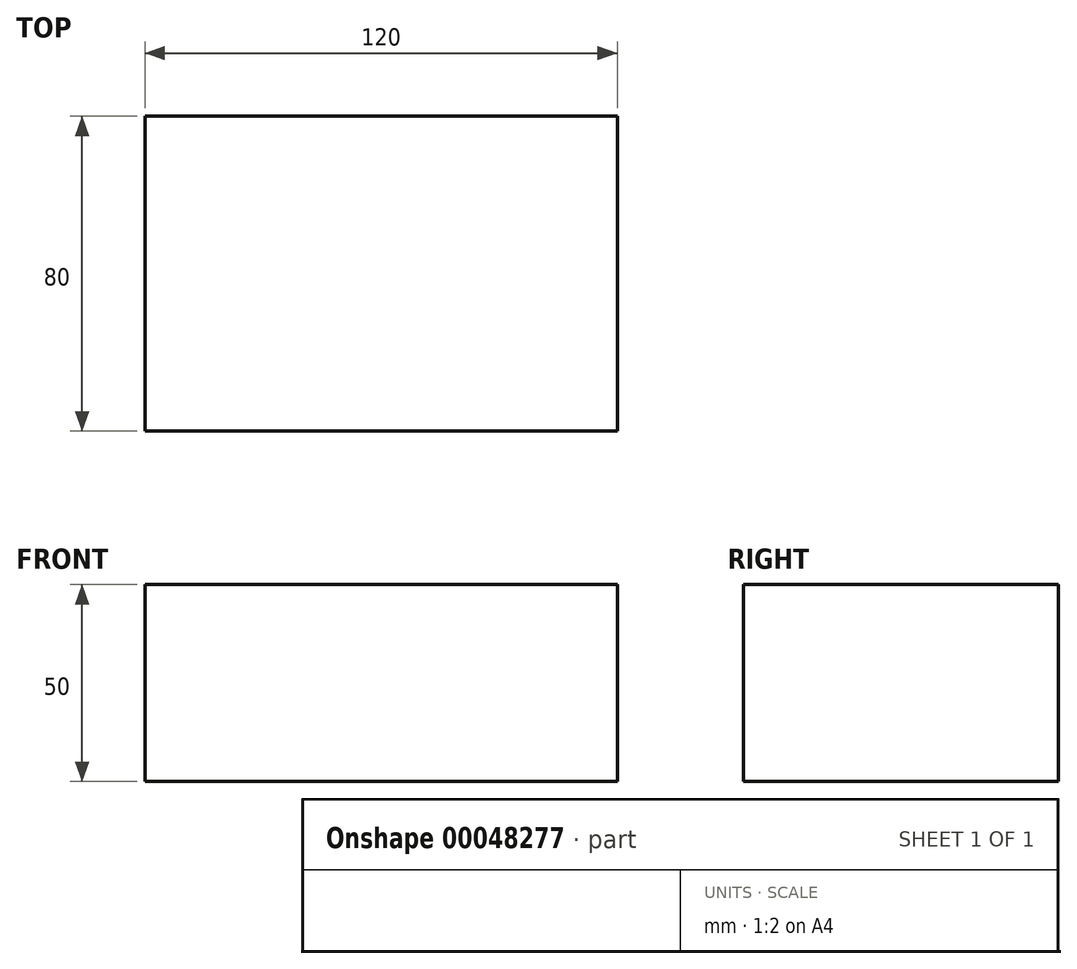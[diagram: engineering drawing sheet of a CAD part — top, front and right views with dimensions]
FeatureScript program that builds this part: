
annotation { "Feature Type Name" : "Feature", "Feature Type Description" : "" }
export const myFeature = defineFeature(function(context is Context, id is Id, definition is map)
    precondition{}
    {
        {
            var Q0;
            Q0=qCreatedBy(makeId("Front.planeOp"),FACE);
            var sketch = newSketch(context, id + "F0", { "sketchPlane" : qUnion([Q0])});
            skLineSegment(sketch, "E0", {"start": v(-60, 50) * mm, "end": v(60, 50) * mm});
            skLineSegment(sketch, "E1", {"start": v(-60, 50) * mm, "end": v(-60, 0) * mm});
            skLineSegment(sketch, "E2", {"start": v(-60, 0) * mm, "end": v(60, 0) * mm});
            skLineSegment(sketch, "E3", {"start": v(60, 0) * mm, "end": v(60, 50) * mm});
            skSolve(sketch);
        }
        {
            var Q0;
            Q0 = qSketchRegion(id + "F0", true);
            extrude(context, id + "F1", {"entities" : qUnion([Q0]), "depth" : 80 * mm});
        }
    });
